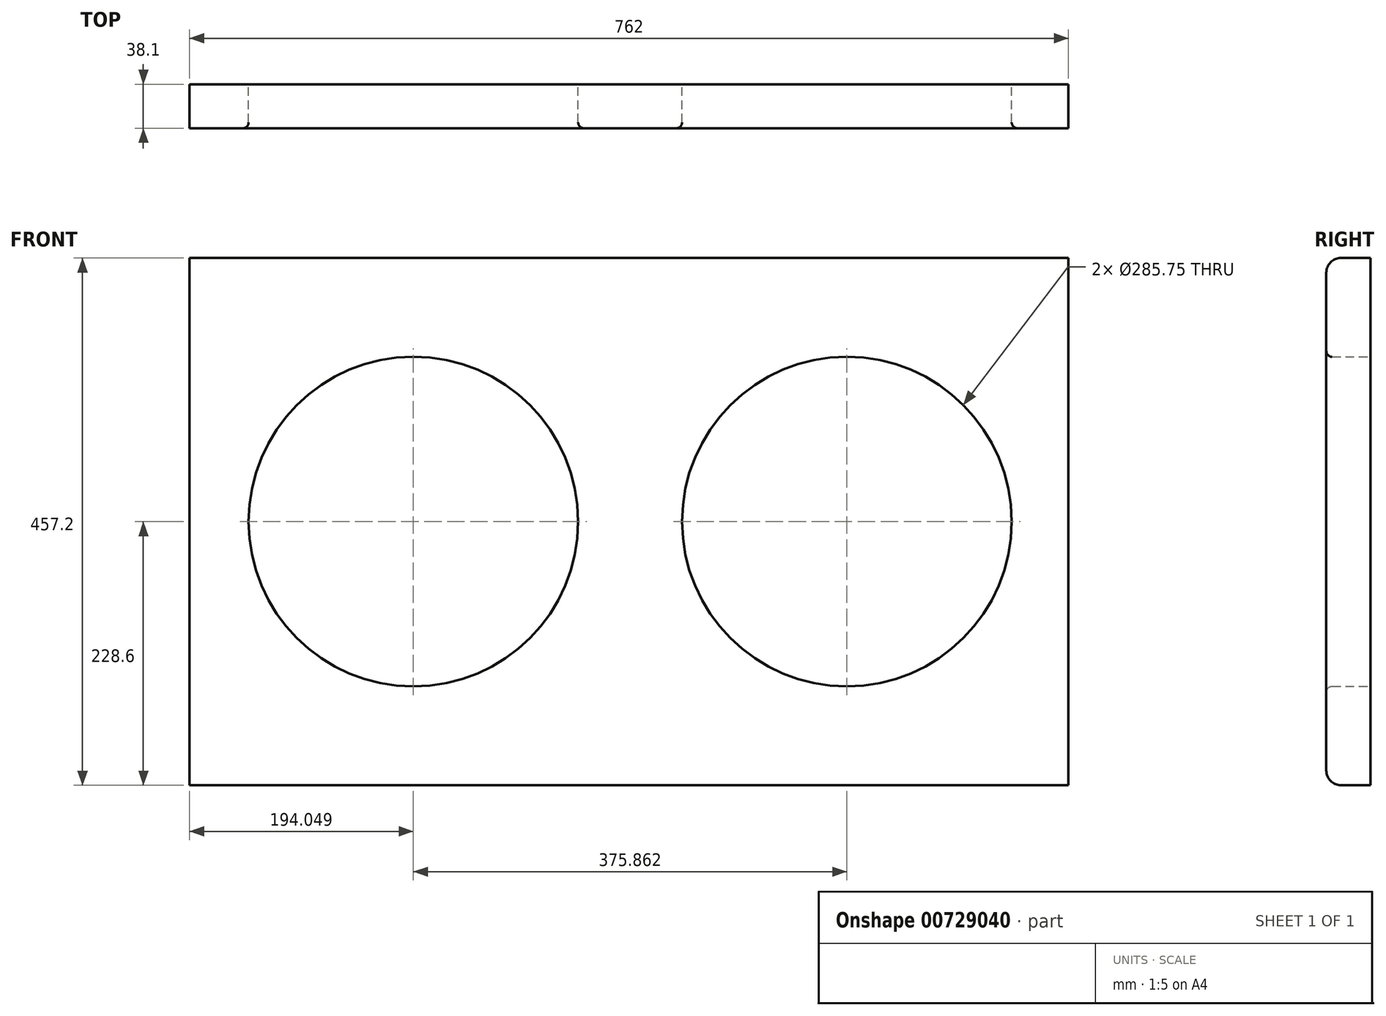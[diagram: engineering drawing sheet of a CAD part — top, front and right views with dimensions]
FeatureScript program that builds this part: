
annotation { "Feature Type Name" : "Feature", "Feature Type Description" : "" }
export const myFeature = defineFeature(function(context is Context, id is Id, definition is map)
    precondition{}
    {
        {
            var Q0;
            Q0=qCreatedBy(makeId("Front.planeOp"),FACE);
            var sketch = newSketch(context, id + "F0", { "sketchPlane" : qUnion([Q0])});
            skLineSegment(sketch, "E0.bottom", {"start": v(381, -228.6) * mm, "end": v(-381, -228.6) * mm});
            skLineSegment(sketch, "E0.top", {"start": v(381, 228.6) * mm, "end": v(-381, 228.6) * mm});
            skLineSegment(sketch, "E0.left", {"start": v(381, -228.6) * mm, "end": v(381, 228.6) * mm});
            skLineSegment(sketch, "E0.right", {"start": v(-381, -228.6) * mm, "end": v(-381, 228.6) * mm});
            skPoint(sketch, "E0.middle", {"position": v(0, 0) * mm});
            skCircle(sketch, "E1", {"center": v(-186.95, 0) * mm, "radius": 142.88 * mm});
            skCircle(sketch, "E2", {"center": v(188.91, 0) * mm, "radius": 142.88 * mm});
            skSolve(sketch);
        }
        {
            var Q0;
            Q0=makeQuery(id+"F0.imprint","IMPRINT",FACE,{"disambiguationData":[TD([[makeQuery(id+"F0.imprint","IMPRINT",EDGE,{"derivedFrom":sQuery(id+"F0.wireOp",EDGE,"E0.bottom")}),-1.0]])]});
            extrude(context, id + "F1", {"entities" : qUnion([Q0]), "depth" : 38.1 * mm, "offsetDistance" : 25.4 * mm});
        }
        {
            var Q0;
            Q0=makeQuery(id+"F1.opExtrude","CAP_EDGE",EDGE,{"disambiguationData":[OSD([sQuery(id+"F0.wireOp",EDGE,"E0.top")])],"isStart":false});
            var Q1;
            Q1=makeQuery(id+"F1.opExtrude","CAP_EDGE",EDGE,{"disambiguationData":[OSD([sQuery(id+"F0.wireOp",EDGE,"E0.bottom")])],"isStart":false});
            fillet(context, id + "F2", {"entities" : qUnion([Q0, Q1]), "radius" : 12.7 * mm, "tangentPropagation" : true, "allowEdgeOverflow" : false});
        }
        {
            var Q0;
            Q0=makeQuery(id+"F1.opExtrude","CAP_EDGE",EDGE,{"disambiguationData":[OSD([sQuery(id+"F0.wireOp",EDGE,"E1")])],"isStart":false});
            var Q1;
            Q1=makeQuery(id+"F1.opExtrude","CAP_EDGE",EDGE,{"disambiguationData":[OSD([sQuery(id+"F0.wireOp",EDGE,"E2")])],"isStart":false});
            fillet(context, id + "F3", {"entities" : qUnion([Q0, Q1]), "radius" : 5.08 * mm, "tangentPropagation" : true, "allowEdgeOverflow" : false});
        }
    });
